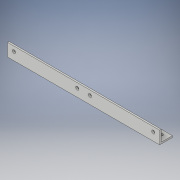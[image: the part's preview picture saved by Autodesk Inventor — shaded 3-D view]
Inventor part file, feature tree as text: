
AUTODESK INVENTOR PART (.ipt)
format: ipt  version: 2017 (Build 210142000, 142)  size: 126,464 bytes
history: native  units: in
note: dims shown in document units (in); Inventor stores cm internally (conversion verified against a paired STEP export)
features: extrude x3, sketch x3
ambient origin geometry x8: Origin, YZ Plane, XZ Plane, XY Plane, X Axis, Y Axis, Z Axis, Center Point
bodies: Solid1 (feature_tree)
feature tree (6):
  extrude  "Extrusion1"  Depth=0.128in
  extrude  "Extrusion2"  Depth=12.0in
  extrude  "Extrusion3"  Depth=12.0in
  sketch  "Sketch1"  dims[d0=1.0in d1=0.128in]
  sketch  "Sketch2"  dims[d2=12.0in d3=0.0in d4=0.628in]
  sketch  "Sketch3"  dims[d5=0.25in d6=0.5in d7=5.5in d8=12.0in d9=0.0in d10=0.628in d11=0.25in d12=0.5in d13=5.5in d14=12.0in d15=0.0in]
